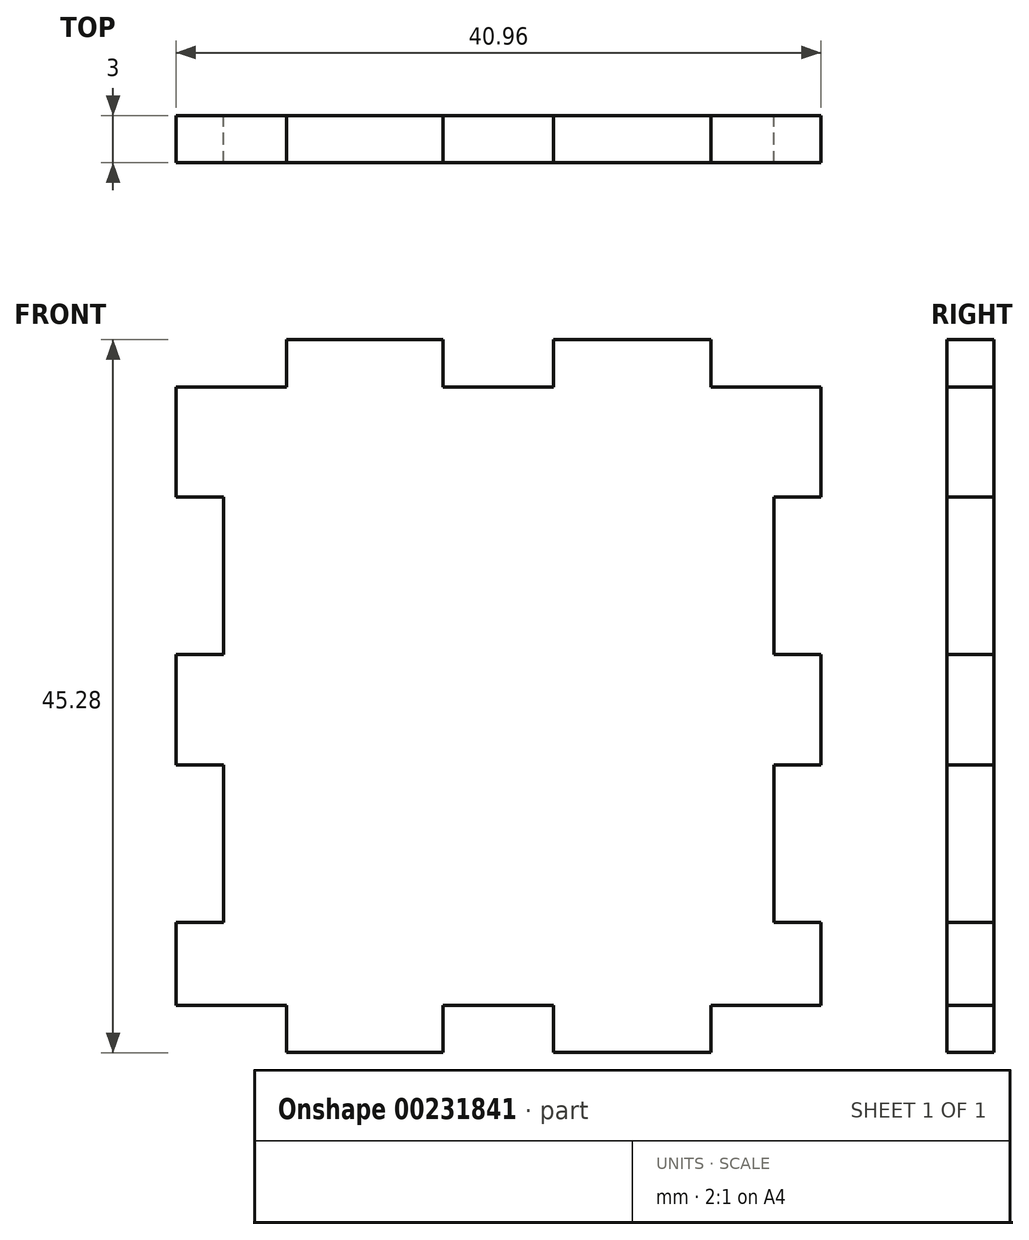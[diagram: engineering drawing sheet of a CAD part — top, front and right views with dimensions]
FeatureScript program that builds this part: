
annotation { "Feature Type Name" : "Feature", "Feature Type Description" : "" }
export const myFeature = defineFeature(function(context is Context, id is Id, definition is map)
    precondition{}
    {
        {
            var Q0;
            Q0=qCreatedBy(makeId("Front.planeOp"),FACE);
            var sketch = newSketch(context, id + "F0", { "sketchPlane" : qUnion([Q0])});
            skLineSegment(sketch, "E0", {"start": v(0, 0) * mm, "end": v(0, 7) * mm});
            skLineSegment(sketch, "E1", {"start": v(0, 7) * mm, "end": v(-3, 7) * mm});
            skLineSegment(sketch, "E2", {"start": v(-3, 7) * mm, "end": v(-3, 17) * mm});
            skLineSegment(sketch, "E3", {"start": v(-3, 17) * mm, "end": v(0, 17) * mm});
            skLineSegment(sketch, "E4", {"start": v(0, 17) * mm, "end": v(0, 24) * mm});
            skLineSegment(sketch, "E5", {"start": v(0, 24) * mm, "end": v(-3, 24) * mm});
            skLineSegment(sketch, "E6", {"start": v(-3, 24) * mm, "end": v(-3, 34) * mm});
            skLineSegment(sketch, "E7", {"start": v(-3, 34) * mm, "end": v(0, 34) * mm});
            skLineSegment(sketch, "E8", {"start": v(0, 34) * mm, "end": v(0, 41) * mm});
            skLineSegment(sketch, "E9", {"start": v(0, 41) * mm, "end": v(-7, 41) * mm});
            skLineSegment(sketch, "E10", {"start": v(-7, 41) * mm, "end": v(-7, 44) * mm});
            skLineSegment(sketch, "E11", {"start": v(-7, 44) * mm, "end": v(-17, 44) * mm});
            skLineSegment(sketch, "E12", {"start": v(-17, 44) * mm, "end": v(-17, 41) * mm});
            skLineSegment(sketch, "E13", {"start": v(-17, 41) * mm, "end": v(-24, 41) * mm});
            skLineSegment(sketch, "E14", {"start": v(-24, 41) * mm, "end": v(-24, 44) * mm});
            skLineSegment(sketch, "E15", {"start": v(-24, 44) * mm, "end": v(-34, 44) * mm});
            skLineSegment(sketch, "E16", {"start": v(-34, 44) * mm, "end": v(-34, 41) * mm});
            skLineSegment(sketch, "E17", {"start": v(-34, 41) * mm, "end": v(-41, 41) * mm});
            skLineSegment(sketch, "E18.MirrorCS", {"start": v(-37.96, 34) * mm, "end": v(-40.96, 34) * mm});
            skLineSegment(sketch, "E19.MirrorCS", {"start": v(-40.96, 7) * mm, "end": v(-37.96, 7) * mm});
            skLineSegment(sketch, "E20.MirrorCS", {"start": v(-33.96, 44) * mm, "end": v(-23.96, 44) * mm});
            skLineSegment(sketch, "E21.MirrorCS", {"start": v(-33.96, 41) * mm, "end": v(-33.96, 44) * mm});
            skLineSegment(sketch, "E22.MirrorCS", {"start": v(-40.96, 24) * mm, "end": v(-37.96, 24) * mm});
            skLineSegment(sketch, "E23.MirrorCS", {"start": v(-37.96, 17) * mm, "end": v(-40.96, 17) * mm});
            skLineSegment(sketch, "E24.MirrorCS", {"start": v(-40.96, 1.72) * mm, "end": v(-40.96, 7) * mm});
            skLineSegment(sketch, "E25.MirrorCS", {"start": v(-37.96, 24) * mm, "end": v(-37.96, 34) * mm});
            skLineSegment(sketch, "E26.MirrorCS", {"start": v(-40.96, 41) * mm, "end": v(-33.96, 41) * mm});
            skLineSegment(sketch, "E27.MirrorCS", {"start": v(-40.96, 17) * mm, "end": v(-40.96, 24) * mm});
            skLineSegment(sketch, "E28.MirrorCS", {"start": v(-40.96, 34) * mm, "end": v(-40.96, 41) * mm});
            skLineSegment(sketch, "E29.MirrorCS", {"start": v(-37.96, 7) * mm, "end": v(-37.96, 17) * mm});
            skLineSegment(sketch, "E30.MirrorCS", {"start": v(-40.96, 1.72) * mm, "end": v(-33.96, 1.72) * mm});
            skLineSegment(sketch, "E31.MirrorCS", {"start": v(-33.96, 1.72) * mm, "end": v(-33.96, -1.28) * mm});
            skLineSegment(sketch, "E32.MirrorCS", {"start": v(-17, -1.28) * mm, "end": v(-17, 1.72) * mm});
            skLineSegment(sketch, "E33.MirrorCS", {"start": v(-24, -1.28) * mm, "end": v(-34, -1.28) * mm});
            skLineSegment(sketch, "E34.MirrorCS", {"start": v(-34, -1.28) * mm, "end": v(-34, 1.72) * mm});
            skLineSegment(sketch, "E35.MirrorCS", {"start": v(0, 1.72) * mm, "end": v(-7, 1.72) * mm});
            skLineSegment(sketch, "E36.MirrorCS", {"start": v(-33.96, -1.28) * mm, "end": v(-23.96, -1.28) * mm});
            skLineSegment(sketch, "E37.MirrorCS", {"start": v(-7, -1.28) * mm, "end": v(-17, -1.28) * mm});
            skLineSegment(sketch, "E38.MirrorCS", {"start": v(-17, 1.72) * mm, "end": v(-24, 1.72) * mm});
            skLineSegment(sketch, "E39.MirrorCS", {"start": v(-24, 1.72) * mm, "end": v(-24, -1.28) * mm});
            skLineSegment(sketch, "E40.MirrorCS", {"start": v(-34, 1.72) * mm, "end": v(-41, 1.72) * mm});
            skLineSegment(sketch, "E41.MirrorCS", {"start": v(-7, 1.72) * mm, "end": v(-7, -1.28) * mm});
            skPoint(sketch, "E42.start.orphan", {"position": v(6.32, 21.36) * mm});
            skPoint(sketch, "E43.orphan", {"position": v(16.69, 21.36) * mm});
            skPoint(sketch, "E44.orphan", {"position": v(-57.64, 21.36) * mm});
            skPoint(sketch, "E45.trimOffspring.end.orphan", {"position": v(-47.28, 21.36) * mm});
            skSolve(sketch);
        }
        {
            var Q0;
            {var subQ5=sQuery(id+"F0.wireOp",EDGE,"E1");Q0=makeQuery(id+"F0.imprint","IMPRINT",FACE,{"disambiguationData":[TD([[makeQuery(id+"F0.imprint","IMPRINT",EDGE,{"derivedFrom":subQ5}),1.0]])]});}
            extrude(context, id + "F1", {"entities" : qUnion([Q0]), "depth" : 3 * mm});
        }
    });
